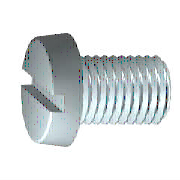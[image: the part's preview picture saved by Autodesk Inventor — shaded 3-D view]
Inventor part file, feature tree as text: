
AUTODESK INVENTOR PART (.ipt)
format: ipt  version: 2023 (Build 270158000, 158)  size: 185,856 bytes
history: native  units: mm (DEFAULTED — no unit token found)
features: sketch x2, extrude x1, plane x1
ambient origin geometry x7: Origin, YZ Plane, XZ Plane, X Axis, Y Axis, Z Axis, Center Point
bodies: Solid1 (feature_tree), Body (feature_tree)
feature tree (4):
  sketch  "Sketch2"  dims[d2=0.766912mm d3=5.0mm d4=8.0mm d5=7.323417mm d8=90.0deg d7=0.0mm d9=13.0mm d10=0.872665mm d11=2.0mm d12=13.0mm d14=0.4mm d15=11.5mm d16=0.0mm d17=0.67658mm d18=0.766912mm d19=2.0mm d20=0.0mm d36=45.0deg d37=0.0mm d39=0.0mm]
  extrude  "Slot"  Depth=11.5mm
  plane  "Work Plane1"
  sketch  "Sketch1"  dims[d0=14.0mm d1=11.5mm]
